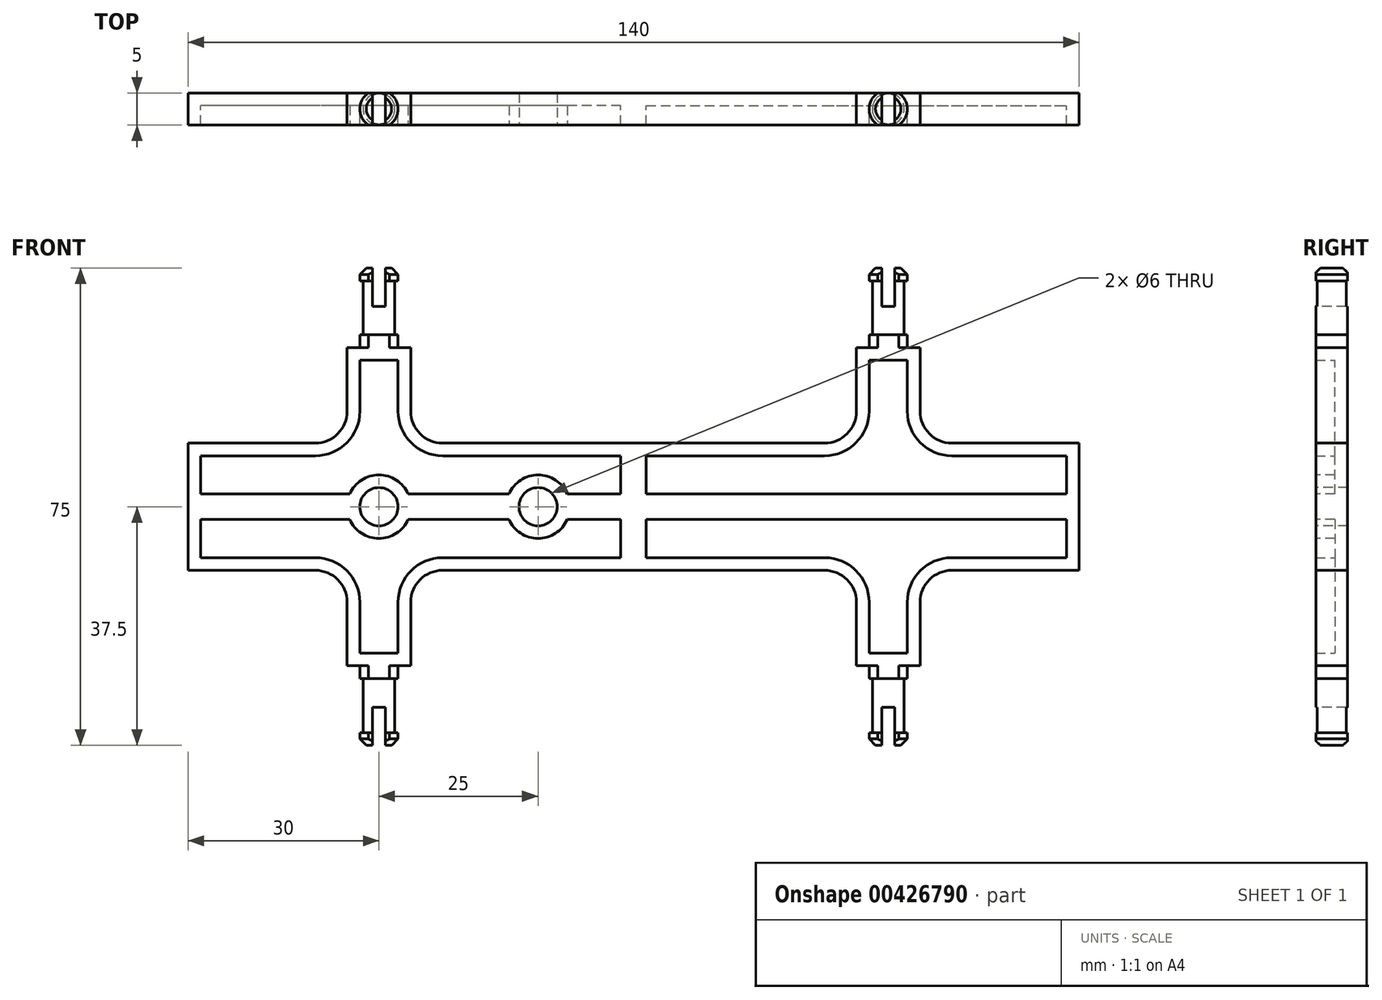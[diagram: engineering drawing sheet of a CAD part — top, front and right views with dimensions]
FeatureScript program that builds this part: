
annotation { "Feature Type Name" : "Feature", "Feature Type Description" : "" }
export const myFeature = defineFeature(function(context is Context, id is Id, definition is map)
    precondition{}
    {
        {
            var Q0;
            Q0=qCreatedBy(makeId("Front.planeOp"),FACE);
            var sketch = newSketch(context, id + "F0", { "sketchPlane" : qUnion([Q0])});
            skLineSegment(sketch, "E0.bottom", {"start": v(0, 0) * mm, "end": v(70, 0) * mm});
            skLineSegment(sketch, "E0.top", {"start": v(0, 10) * mm, "end": v(30, 10) * mm});
            skLineSegment(sketch, "E0.left", {"start": v(0, 0) * mm, "end": v(0, 10) * mm});
            skLineSegment(sketch, "E0.right", {"start": v(70, 0) * mm, "end": v(70, 10) * mm});
            skLineSegment(sketch, "E1.top", {"start": v(35, 25) * mm, "end": v(45, 25) * mm});
            skLineSegment(sketch, "E1.left", {"start": v(35, 15) * mm, "end": v(35, 25) * mm});
            skLineSegment(sketch, "E1.right", {"start": v(45, 15) * mm, "end": v(45, 25) * mm});
            skLineSegment(sketch, "E2.trimOffspring", {"start": v(50, 10) * mm, "end": v(70, 10) * mm});
            skPoint(sketch, "E3.visualSharp", {"position": v(35, 10) * mm});
            skArc(sketch, "E3.filletArc", {"start": v(30, 10) * mm, "mid": v(33.54, 11.46) * mm, "end": v(35, 15) * mm});
            skPoint(sketch, "E4.visualSharp", {"position": v(45, 10) * mm});
            skArc(sketch, "E4.filletArc", {"start": v(45, 15) * mm, "mid": v(46.46, 11.46) * mm, "end": v(50, 10) * mm});
            skSolve(sketch);
        }
        {
            var Q0;
            Q0 = qSketchRegion(id + "F0", true);
            extrude(context, id + "F1", {"entities" : qUnion([Q0]), "endBound" : BoundingType.SYMMETRIC, "depth" : 5 * mm});
        }
        {
            var Q0;
            Q0=makeQuery(id+"F1.opExtrude","CAP_FACE",FACE,{"disambiguationData":[OSD([sQuery(id+"F0.wireOp",EDGE,"E0.bottom"),sQuery(id+"F0.wireOp",EDGE,"E0.top"),sQuery(id+"F0.wireOp",EDGE,"E0.left"),sQuery(id+"F0.wireOp",EDGE,"E0.right"),sQuery(id+"F0.wireOp",EDGE,"E1.top"),sQuery(id+"F0.wireOp",EDGE,"E1.left"),sQuery(id+"F0.wireOp",EDGE,"E1.right"),sQuery(id+"F0.wireOp",EDGE,"E2.trimOffspring"),sQuery(id+"F0.wireOp",EDGE,"E3.filletArc"),sQuery(id+"F0.wireOp",EDGE,"E4.filletArc")])],"isStart":false});
            shell(context, id + "F2", {"entities" : qUnion([Q0]), "thickness" : 2 * mm});
        }
        {
            var Q0;
            Q0=qCreatedBy(makeId("Front.planeOp"),FACE);
            var sketch = newSketch(context, id + "F3", { "sketchPlane" : qUnion([Q0])});
            skLineSegment(sketch, "E5", {"start": v(37, 25) * mm, "end": v(37, 27) * mm});
            skLineSegment(sketch, "E6", {"start": v(37, 27) * mm, "end": v(37.5, 27) * mm});
            skLineSegment(sketch, "E7", {"start": v(37.5, 27) * mm, "end": v(37.5, 35.5) * mm});
            skLineSegment(sketch, "E8", {"start": v(37.5, 35.5) * mm, "end": v(37, 35.5) * mm});
            skLineSegment(sketch, "E9", {"start": v(37, 35.5) * mm, "end": v(37, 37.5) * mm});
            skLineSegment(sketch, "E10", {"start": v(37, 37.5) * mm, "end": v(40, 37.5) * mm});
            skLineSegment(sketch, "E11", {"start": v(40, 37.5) * mm, "end": v(40, 25) * mm});
            skLineSegment(sketch, "E12", {"start": v(40, 25) * mm, "end": v(37, 25) * mm});
            skSolve(sketch);
        }
        {
            var Q0;
            Q0 = qSketchRegion(id + "F3", true);
            var Q1;
            Q1=sQuery(id+"F3.wireOp",EDGE,"E11");
            revolve(context, id + "F4", {"operationType" : NewBodyOperationType.ADD, "entities" : qUnion([Q0]), "axis" : qUnion([Q1]), "revolveType" : RevolveType.FULL});
        }
        {
            var Q0;
            Q0=makeQuery(id+"F4.opRevolve","SWEPT_EDGE",EDGE,{"disambiguationData":[OSD([sQuery(id+"F3.wireOp",EDGE,"E9"),sQuery(id+"F3.wireOp",EDGE,"E10")])]});
            chamfer(context, id + "F5", {"entities" : qUnion([Q0]), "width" : 1 * mm, "tangentPropagation" : true});
        }
        {
            var Q0;
            Q0=makeQuery(id+"F4.opRevolve","SWEPT_FACE",FACE,{"disambiguationData":[OSD([sQuery(id+"F3.wireOp",EDGE,"E10")])]});
            var sketch = newSketch(context, id + "F6", { "sketchPlane" : qUnion([Q0])});
            skLineSegment(sketch, "E13.bottom", {"start": v(-5.21, 2.5) * mm, "end": v(76.9, 2.5) * mm});
            skLineSegment(sketch, "E13.top", {"start": v(-5.21, -2.5) * mm, "end": v(76.9, -2.5) * mm});
            skLineSegment(sketch, "E13.left", {"start": v(-5.21, 2.5) * mm, "end": v(-5.21, -2.5) * mm});
            skLineSegment(sketch, "E13.right", {"start": v(76.9, 2.5) * mm, "end": v(76.9, -2.5) * mm});
            skSolve(sketch);
        }
        {
            var Q0;
            Q0 = qSketchRegion(id + "F6", true);
            extrude(context, id + "F7", {"entities" : qUnion([Q0]), "operationType" : NewBodyOperationType.INTERSECT, "endBound" : BoundingType.THROUGH_ALL, "oppositeDirection" : true, "depth" : 25 * mm});
        }
        {
            var Q0;
            Q0=makeQuery(id+"F4.opRevolve","SWEPT_FACE",FACE,{"disambiguationData":[OSD([sQuery(id+"F3.wireOp",EDGE,"E10")])]});
            var sketch = newSketch(context, id + "F8", { "sketchPlane" : qUnion([Q0])});
            skLineSegment(sketch, "E14.bottom", {"start": v(39, 3.45) * mm, "end": v(41, 3.45) * mm});
            skLineSegment(sketch, "E14.top", {"start": v(39, -4.11) * mm, "end": v(41, -4.11) * mm});
            skLineSegment(sketch, "E14.left", {"start": v(39, 3.45) * mm, "end": v(39, -4.11) * mm});
            skLineSegment(sketch, "E14.right", {"start": v(41, 3.45) * mm, "end": v(41, -4.11) * mm});
            skSolve(sketch);
        }
        {
            var Q0;
            Q0 = qSketchRegion(id + "F8", true);
            extrude(context, id + "F9", {"entities" : qUnion([Q0]), "operationType" : NewBodyOperationType.REMOVE, "oppositeDirection" : true, "depth" : 6 * mm});
        }
        {
            var Q0;
            Q0=makeQuery(id+"F1.opExtrude","SWEPT_BODY",BODY,{"disambiguationData":[OSD([sQuery(id+"F0.wireOp",EDGE,"E0.bottom"),sQuery(id+"F0.wireOp",EDGE,"E0.top"),sQuery(id+"F0.wireOp",EDGE,"E0.left"),sQuery(id+"F0.wireOp",EDGE,"E0.right"),sQuery(id+"F0.wireOp",EDGE,"E1.top"),sQuery(id+"F0.wireOp",EDGE,"E1.left"),sQuery(id+"F0.wireOp",EDGE,"E1.right"),sQuery(id+"F0.wireOp",EDGE,"E2.trimOffspring"),sQuery(id+"F0.wireOp",EDGE,"E3.filletArc"),sQuery(id+"F0.wireOp",EDGE,"E4.filletArc")])]});
            var Q1;
            Q1=qCreatedBy(makeId("Top.planeOp"),FACE);
            mirror(context, id + "F10", {"operationType" : NewBodyOperationType.ADD, "entities" : qUnion([Q0]), "mirrorPlane" : qUnion([Q1])});
        }
        {
            var Q0;
            Q0=makeQuery(id+"F1.opExtrude","SWEPT_BODY",BODY,{"disambiguationData":[OSD([sQuery(id+"F0.wireOp",EDGE,"E0.bottom"),sQuery(id+"F0.wireOp",EDGE,"E0.top"),sQuery(id+"F0.wireOp",EDGE,"E0.left"),sQuery(id+"F0.wireOp",EDGE,"E0.right"),sQuery(id+"F0.wireOp",EDGE,"E1.top"),sQuery(id+"F0.wireOp",EDGE,"E1.left"),sQuery(id+"F0.wireOp",EDGE,"E1.right"),sQuery(id+"F0.wireOp",EDGE,"E2.trimOffspring"),sQuery(id+"F0.wireOp",EDGE,"E3.filletArc"),sQuery(id+"F0.wireOp",EDGE,"E4.filletArc")])]});
            var Q1;
            Q1=qCreatedBy(makeId("Right.planeOp"),FACE);
            mirror(context, id + "F11", {"operationType" : NewBodyOperationType.ADD, "entities" : qUnion([Q0]), "mirrorPlane" : qUnion([Q1])});
        }
        {
            var Q0;
            {var subQ0=makeQuery(id+"F7.boolean.opBoolean","MERGE",FACE,{"derivedFrom":[makeQuery(id+"F1.opExtrude","CAP_FACE",FACE,{"disambiguationData":[OSD([sQuery(id+"F0.wireOp",EDGE,"E0.bottom"),sQuery(id+"F0.wireOp",EDGE,"E0.top"),sQuery(id+"F0.wireOp",EDGE,"E0.left"),sQuery(id+"F0.wireOp",EDGE,"E0.right"),sQuery(id+"F0.wireOp",EDGE,"E1.top"),sQuery(id+"F0.wireOp",EDGE,"E1.left"),sQuery(id+"F0.wireOp",EDGE,"E1.right"),sQuery(id+"F0.wireOp",EDGE,"E2.trimOffspring"),sQuery(id+"F0.wireOp",EDGE,"E3.filletArc"),sQuery(id+"F0.wireOp",EDGE,"E4.filletArc")])],"isStart":false}),makeQuery(id+"F7.boolean.toolComplement.opBoolean","COPY",FACE,{"derivedFrom":makeQuery(id+"F7.opExtrude","SWEPT_FACE",FACE,{"disambiguationData":[OSD([sQuery(id+"F6.wireOp",EDGE,"E13.top")])]})})]});var subQ1=makeQuery(id+"F10.boolean.opBoolean","MERGE",FACE,{"derivedFrom":[subQ0,makeQuery(id+"F10.opPattern","COPY",FACE,{"derivedFrom":subQ0,"instanceName":"1"})]});Q0=makeQuery(id+"F11.boolean.opBoolean","MERGE",FACE,{"derivedFrom":[subQ1,makeQuery(id+"F11.opPattern","COPY",FACE,{"derivedFrom":subQ1,"instanceName":"1"})]});}
            var sketch = newSketch(context, id + "F12", { "sketchPlane" : qUnion([Q0])});
            skCircle(sketch, "E15", {"center": v(-40, 0) * mm, "radius": 5 * mm});
            skCircle(sketch, "E16", {"center": v(-15, 0) * mm, "radius": 5 * mm});
            skSolve(sketch);
        }
        {
            var Q0;
            Q0 = qSketchRegion(id + "F12", true);
            extrude(context, id + "F13", {"entities" : qUnion([Q0]), "operationType" : NewBodyOperationType.ADD, "endBound" : BoundingType.UP_TO_NEXT, "oppositeDirection" : true, "depth" : 25 * mm});
        }
        {
            var Q0;
            {var subQ0=makeQuery(id+"F7.boolean.opBoolean","MERGE",FACE,{"derivedFrom":[makeQuery(id+"F1.opExtrude","CAP_FACE",FACE,{"disambiguationData":[OSD([sQuery(id+"F0.wireOp",EDGE,"E0.bottom"),sQuery(id+"F0.wireOp",EDGE,"E0.top"),sQuery(id+"F0.wireOp",EDGE,"E0.left"),sQuery(id+"F0.wireOp",EDGE,"E0.right"),sQuery(id+"F0.wireOp",EDGE,"E1.top"),sQuery(id+"F0.wireOp",EDGE,"E1.left"),sQuery(id+"F0.wireOp",EDGE,"E1.right"),sQuery(id+"F0.wireOp",EDGE,"E2.trimOffspring"),sQuery(id+"F0.wireOp",EDGE,"E3.filletArc"),sQuery(id+"F0.wireOp",EDGE,"E4.filletArc")])],"isStart":false}),makeQuery(id+"F7.boolean.toolComplement.opBoolean","COPY",FACE,{"derivedFrom":makeQuery(id+"F7.opExtrude","SWEPT_FACE",FACE,{"disambiguationData":[OSD([sQuery(id+"F6.wireOp",EDGE,"E13.top")])]})})]});var subQ1=makeQuery(id+"F10.boolean.opBoolean","MERGE",FACE,{"derivedFrom":[subQ0,makeQuery(id+"F10.opPattern","COPY",FACE,{"derivedFrom":subQ0,"instanceName":"1"})]});Q0=makeQuery(id+"F13.boolean.opBoolean","MERGE",FACE,{"derivedFrom":[makeQuery(id+"F11.boolean.opBoolean","MERGE",FACE,{"derivedFrom":[subQ1,makeQuery(id+"F11.opPattern","COPY",FACE,{"derivedFrom":subQ1,"instanceName":"1"})]}),makeQuery(id+"F13.opExtrude","CAP_FACE",FACE,{"disambiguationData":[OSD([sQuery(id+"F12.wireOp",EDGE,"E15")])],"isStart":true}),makeQuery(id+"F13.opExtrude","CAP_FACE",FACE,{"disambiguationData":[OSD([sQuery(id+"F12.wireOp",EDGE,"E16")])],"isStart":true})]});}
            var sketch = newSketch(context, id + "F14", { "sketchPlane" : qUnion([Q0])});
            skPoint(sketch, "E17", {"position": v(-40, 0) * mm});
            skPoint(sketch, "E18", {"position": v(-15, 0) * mm});
            skSolve(sketch);
        }
        {
            var Q0;
            Q0=sQuery(id+"F14.wireOp",VERTEX,"E17");
            var Q1;
            Q1=sQuery(id+"F14.wireOp",VERTEX,"E18");
            var Q2;
            Q2=makeQuery(id+"F1.opExtrude","SWEPT_BODY",BODY,{"disambiguationData":[OSD([sQuery(id+"F0.wireOp",EDGE,"E0.bottom"),sQuery(id+"F0.wireOp",EDGE,"E0.top"),sQuery(id+"F0.wireOp",EDGE,"E0.left"),sQuery(id+"F0.wireOp",EDGE,"E0.right"),sQuery(id+"F0.wireOp",EDGE,"E1.top"),sQuery(id+"F0.wireOp",EDGE,"E1.left"),sQuery(id+"F0.wireOp",EDGE,"E1.right"),sQuery(id+"F0.wireOp",EDGE,"E2.trimOffspring"),sQuery(id+"F0.wireOp",EDGE,"E3.filletArc"),sQuery(id+"F0.wireOp",EDGE,"E4.filletArc")])]});
            hole(context, id + "F15", {"style" : HoleStyle.SIMPLE, "endStyle" : HoleEndStyle.THROUGH, "holeDiameter" : 6 * mm, "isTappedThrough" : true, "tappedDepth" : 12 * mm, "tapClearance" : 3, "locations" : qUnion([Q0, Q1]), "scope" : qUnion([Q2])});
        }
    });
